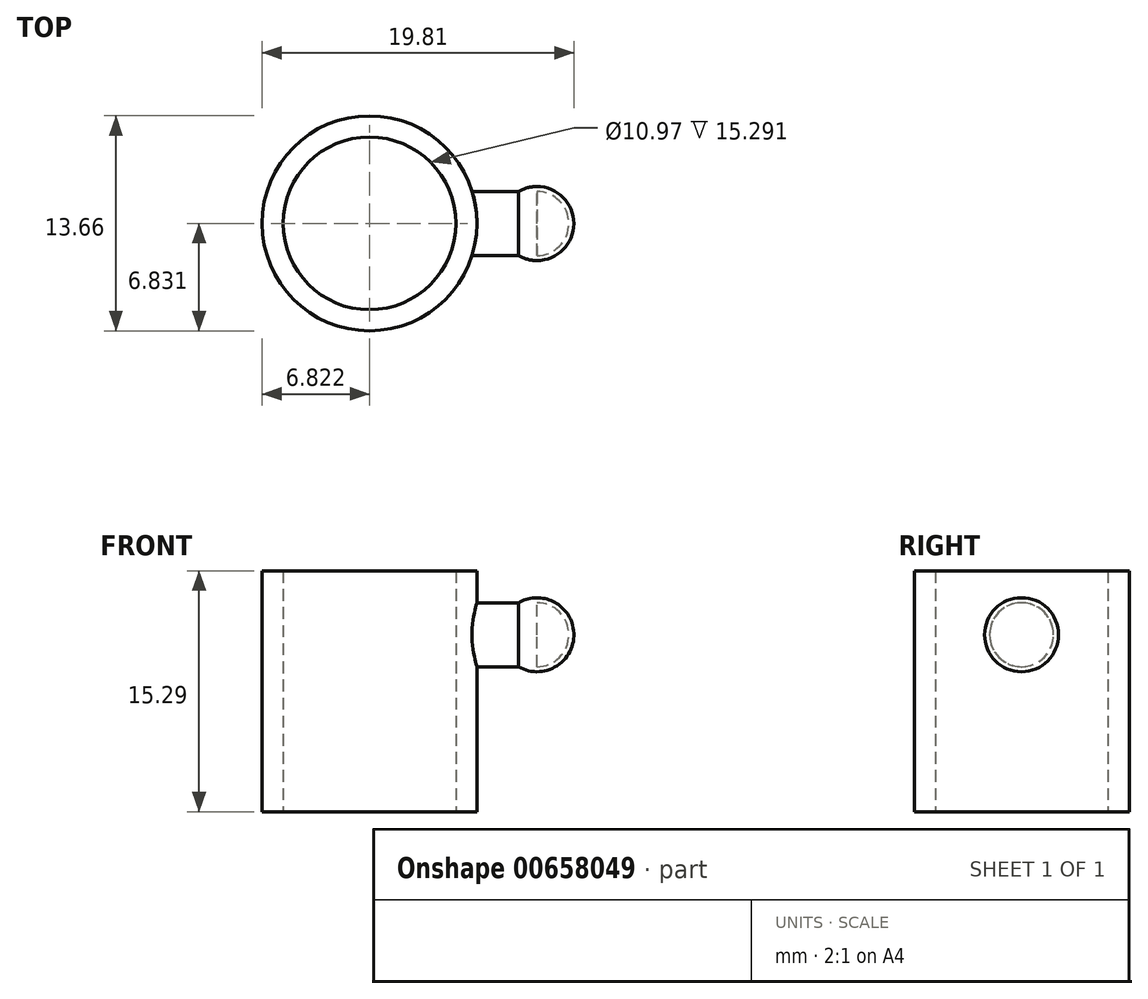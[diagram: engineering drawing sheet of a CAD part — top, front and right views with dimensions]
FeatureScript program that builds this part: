
annotation { "Feature Type Name" : "Feature", "Feature Type Description" : "" }
export const myFeature = defineFeature(function(context is Context, id is Id, definition is map)
    precondition{}
    {
        {
            var Q0;
            Q0=qCreatedBy(makeId("Top.planeOp"),FACE);
            var sketch = newSketch(context, id + "F0", { "sketchPlane" : qUnion([Q0])});
            skCircle(sketch, "E0.0", {"center": v(-43.27, 13.76) * mm, "radius": 6.83 * mm});
            skCircle(sketch, "E1.0", {"center": v(-43.27, 13.76) * mm, "radius": 5.48 * mm});
            skSolve(sketch);
        }
        {
            var Q0;
            Q0 = qSketchRegion(id + "F0", true);
            extrude(context, id + "F1", {"entities" : qUnion([Q0]), "depth" : 15.3 * mm, "offsetDistance" : 25.4 * mm});
        }
        {
            var Q0;
            Q0=qCreatedBy(makeId("Right.planeOp"),FACE);
            cPlane(context, id + "F2", {"entities" : qUnion([Q0]), "cplaneType" : CPlaneType.OFFSET, "offset" : 35.53 * mm, "oppositeDirection" : true, "width" : 152.4 * mm, "height" : 152.4 * mm});
        }
        {
            var Q0;
            Q0=qCreatedBy(id+"F2.planeOp",FACE);
            var sketch = newSketch(context, id + "F3", { "sketchPlane" : qUnion([Q0])});
            skCircle(sketch, "E2", {"center": v(13.75, 11.24) * mm, "radius": 2.03 * mm});
            skPoint(sketch, "E3.start.orphan", {"position": v(5.99, 0) * mm});
            skPoint(sketch, "E4.end.orphan", {"position": v(21.4, 0) * mm});
            skSolve(sketch);
        }
        {
            var Q0;
            Q0=makeQuery(id+"F3.imprint","IMPRINT",FACE,{"disambiguationData":[TD([[makeQuery(id+"F3.imprint","IMPRINT",EDGE,{"derivedFrom":sQuery(id+"F3.wireOp",EDGE,"E2")}),1.0]])]});
            extrude(context, id + "F4", {"entities" : qUnion([Q0]), "operationType" : NewBodyOperationType.ADD, "depth" : 2.9 * mm, "offsetDistance" : 25.4 * mm, "hasSecondDirection" : true, "secondDirectionOppositeDirection" : true, "secondDirectionDepth" : 1.63 * mm});
        }
        {
            var Q0;
            Q0=makeQuery(id+"F4.opExtrude","CAP_FACE",FACE,{"disambiguationData":[OSD([sQuery(id+"F3.wireOp",EDGE,"E2")])],"isStart":false});
            var sketch = newSketch(context, id + "F5", { "sketchPlane" : qUnion([Q0])});
            skLineSegment(sketch, "E5", {"start": v(13.75, 11.24) * mm, "end": v(11.4, 11.24) * mm});
            skLineSegment(sketch, "E6", {"start": v(13.75, 11.24) * mm, "end": v(16.1, 11.24) * mm});
            skArc(sketch, "E7.0", {"start": v(16.1, 11.24) * mm, "mid": v(13.75, 13.59) * mm, "end": v(11.4, 11.24) * mm});
            skSolve(sketch);
        }
        {
            var Q0;
            {var subQ0=sQuery(id+"F5.wireOp",EDGE,"E7.0");Q0=makeQuery(id+"F5.imprint","IMPRINT",FACE,{"disambiguationData":[TD([[makeQuery(id+"F5.imprint","IMPRINT",EDGE,{"derivedFrom":subQ0}),1.0]])]});}
            var Q1;
            Q1=sQuery(id+"F5.wireOp",EDGE,"E5");
            revolve(context, id + "F6", {"operationType" : NewBodyOperationType.ADD, "entities" : qUnion([Q0]), "axis" : qUnion([Q1]), "revolveType" : RevolveType.FULL});
        }
    });
